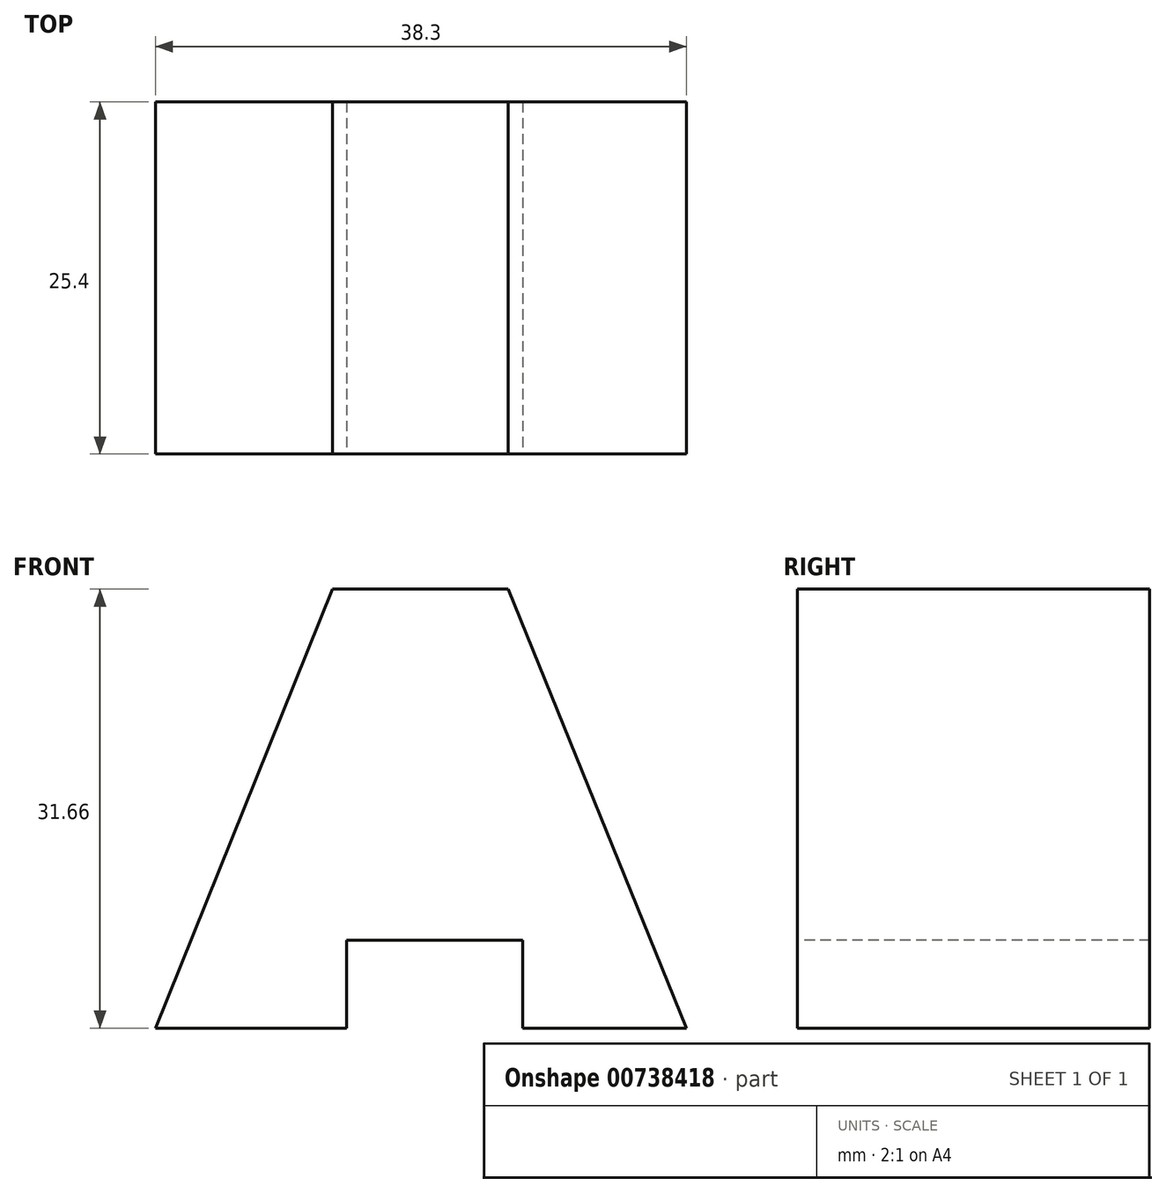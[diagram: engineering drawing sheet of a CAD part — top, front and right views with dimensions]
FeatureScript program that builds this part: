
annotation { "Feature Type Name" : "Feature", "Feature Type Description" : "" }
export const myFeature = defineFeature(function(context is Context, id is Id, definition is map)
    precondition{}
    {
        {
            var Q0;
            Q0=qCreatedBy(makeId("Front.planeOp"),FACE);
            var sketch = newSketch(context, id + "F0", { "sketchPlane" : qUnion([Q0])});
            skLineSegment(sketch, "E0", {"start": v(0, 0) * mm, "end": v(38.3, 0) * mm});
            skLineSegment(sketch, "E1", {"start": v(38.3, 0) * mm, "end": v(38.3, 31.66) * mm});
            skLineSegment(sketch, "E2", {"start": v(38.3, 31.66) * mm, "end": v(0, 31.66) * mm});
            skLineSegment(sketch, "E3", {"start": v(0, 31.66) * mm, "end": v(0, 0) * mm});
            skSolve(sketch);
        }
        {
            var Q0;
            Q0 = qSketchRegion(id + "F0", true);
            extrude(context, id + "F1", {"entities" : qUnion([Q0]), "depth" : 25.4 * mm, "offsetDistance" : 25.4 * mm});
        }
        {
            var Q0;
            Q0=makeQuery(id+"F1.opExtrude","CAP_FACE",FACE,{"disambiguationData":[OSD([sQuery(id+"F0.wireOp",EDGE,"E0"),sQuery(id+"F0.wireOp",EDGE,"E1"),sQuery(id+"F0.wireOp",EDGE,"E2"),sQuery(id+"F0.wireOp",EDGE,"E3")])],"isStart":false});
            var sketch = newSketch(context, id + "F2", { "sketchPlane" : qUnion([Q0])});
            skLineSegment(sketch, "E4", {"start": v(0, 0) * mm, "end": v(12.77, 0) * mm});
            skLineSegment(sketch, "E5", {"start": v(12.77, 0) * mm, "end": v(12.77, 31.66) * mm});
            skLineSegment(sketch, "E6", {"start": v(12.77, 31.66) * mm, "end": v(0, 0) * mm});
            skSolve(sketch);
        }
        {
            var Q0;
            {var subQ0=sQuery(id+"F2.wireOp",EDGE,"E6");Q0=makeQuery(id+"F2.imprint","IMPRINT",FACE,{"disambiguationData":[TD([[makeQuery(id+"F2.imprint","IMPRINT",EDGE,{"derivedFrom":subQ0}),-1.0]])]});}
            extrude(context, id + "F3", {"entities" : qUnion([Q0]), "operationType" : NewBodyOperationType.REMOVE, "endBound" : BoundingType.THROUGH_ALL, "oppositeDirection" : true, "depth" : 25.4 * mm, "offsetDistance" : 25.4 * mm});
        }
        {
            var Q0;
            Q0=makeQuery(id+"F1.opExtrude","CAP_FACE",FACE,{"disambiguationData":[OSD([sQuery(id+"F0.wireOp",EDGE,"E0"),sQuery(id+"F0.wireOp",EDGE,"E1"),sQuery(id+"F0.wireOp",EDGE,"E2"),sQuery(id+"F0.wireOp",EDGE,"E3")])],"isStart":false});
            var sketch = newSketch(context, id + "F4", { "sketchPlane" : qUnion([Q0])});
            skLineSegment(sketch, "E7", {"start": v(38.3, 0) * mm, "end": v(25.43, 0) * mm});
            skLineSegment(sketch, "E8", {"start": v(25.43, 0) * mm, "end": v(25.43, 31.66) * mm});
            skLineSegment(sketch, "E9", {"start": v(25.43, 31.66) * mm, "end": v(38.3, 0) * mm});
            skSolve(sketch);
        }
        {
            var Q0;
            {var subQ0=sQuery(id+"F4.wireOp",EDGE,"E9");Q0=makeQuery(id+"F4.imprint","IMPRINT",FACE,{"disambiguationData":[TD([[makeQuery(id+"F4.imprint","IMPRINT",EDGE,{"derivedFrom":subQ0}),1.0]])]});}
            extrude(context, id + "F5", {"entities" : qUnion([Q0]), "operationType" : NewBodyOperationType.ADD, "depth" : 25.4 * mm, "offsetDistance" : 25.4 * mm});
        }
        {
            var Q0;
            Q0=makeQuery(id+"F5.opExtrude","CAP_FACE",FACE,{"disambiguationData":[OSD([sQuery(id+"F0.wireOp",EDGE,"E1"),sQuery(id+"F0.wireOp",EDGE,"E2"),sQuery(id+"F4.wireOp",EDGE,"E9")])],"isStart":false});
            extrude(context, id + "F6", {"entities" : qUnion([Q0]), "operationType" : NewBodyOperationType.REMOVE, "endBound" : BoundingType.THROUGH_ALL, "oppositeDirection" : true, "depth" : 25.4 * mm, "offsetDistance" : 25.4 * mm});
        }
        {
            var Q0;
            Q0=makeQuery(id+"F1.opExtrude","CAP_FACE",FACE,{"disambiguationData":[OSD([sQuery(id+"F0.wireOp",EDGE,"E0"),sQuery(id+"F0.wireOp",EDGE,"E1"),sQuery(id+"F0.wireOp",EDGE,"E2"),sQuery(id+"F0.wireOp",EDGE,"E3")])],"isStart":false});
            var sketch = newSketch(context, id + "F7", { "sketchPlane" : qUnion([Q0])});
            skLineSegment(sketch, "E10", {"start": v(13.77, 6.35) * mm, "end": v(13.77, 0) * mm});
            skPoint(sketch, "E10.endSnap0", {"position": v(19.15, 0) * mm});
            skLineSegment(sketch, "E11", {"start": v(13.77, 6.35) * mm, "end": v(26.47, 6.35) * mm});
            skLineSegment(sketch, "E12", {"start": v(26.47, 6.35) * mm, "end": v(26.47, 0) * mm});
            skSolve(sketch);
        }
        {
            var Q0;
            {var subQ0=sQuery(id+"F7.wireOp",EDGE,"E10");Q0=makeQuery(id+"F7.imprint","IMPRINT",FACE,{"disambiguationData":[TD([[makeQuery(id+"F7.imprint","IMPRINT",EDGE,{"derivedFrom":subQ0}),1.0]])]});}
            extrude(context, id + "F8", {"entities" : qUnion([Q0]), "operationType" : NewBodyOperationType.REMOVE, "oppositeDirection" : true, "depth" : 25.4 * mm, "offsetDistance" : 25.4 * mm});
        }
    });
